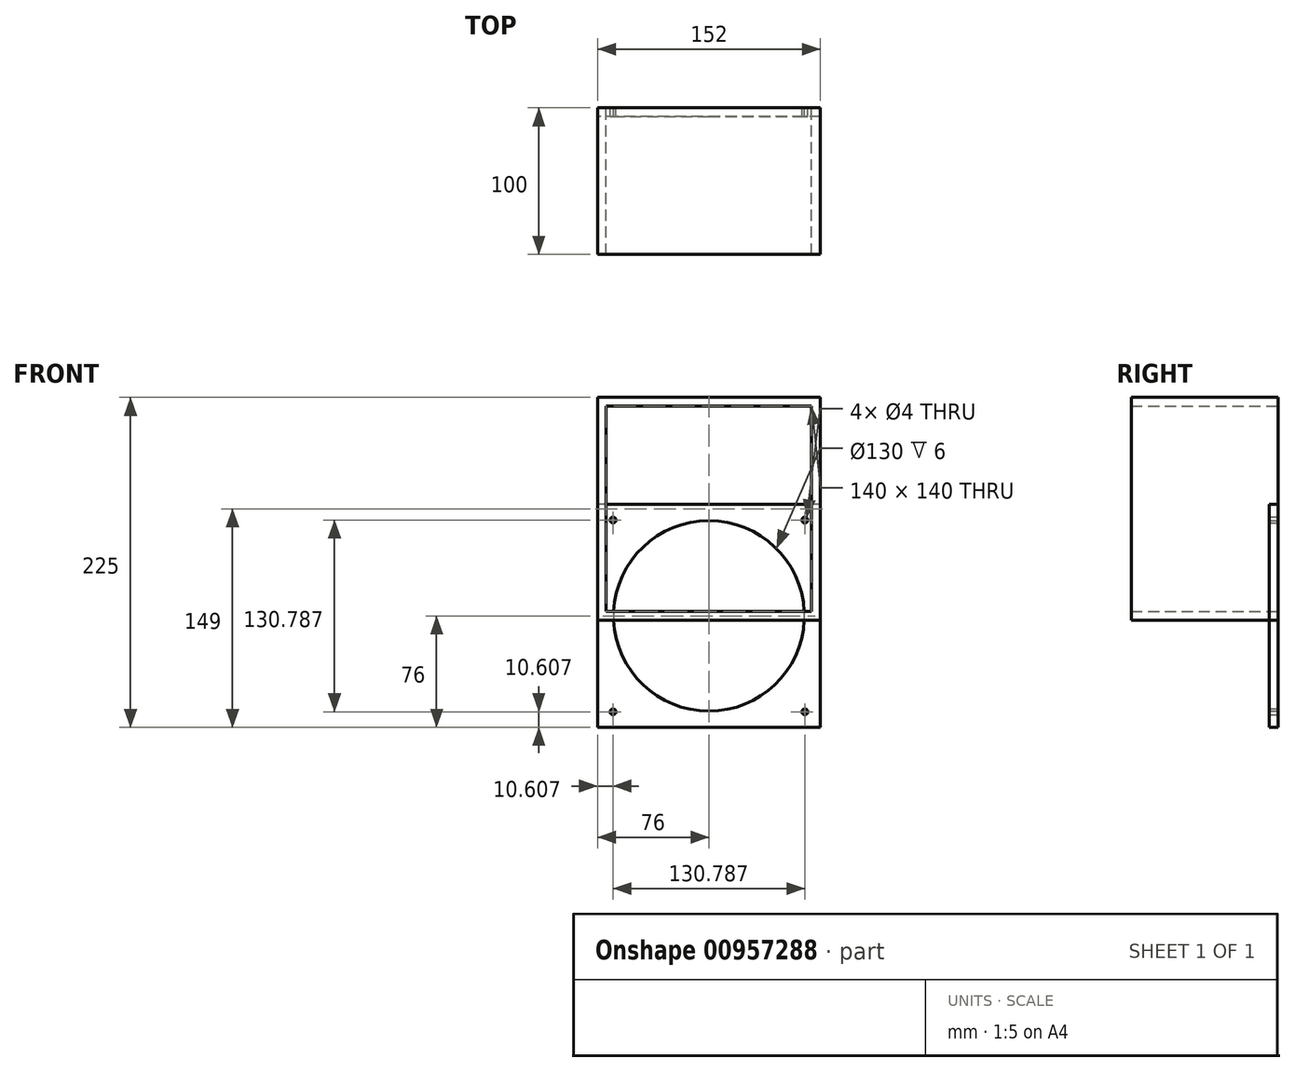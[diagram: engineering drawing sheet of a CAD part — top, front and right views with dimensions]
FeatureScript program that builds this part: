
annotation { "Feature Type Name" : "Feature", "Feature Type Description" : "" }
export const myFeature = defineFeature(function(context is Context, id is Id, definition is map)
    precondition{}
    {
        {
            var Q0;
            Q0=qCreatedBy(makeId("Front.planeOp"),FACE);
            var sketch = newSketch(context, id + "F0", { "sketchPlane" : qUnion([Q0])});
            skLineSegment(sketch, "E0.bottom", {"start": v(70, 3) * mm, "end": v(-70, 3) * mm});
            skLineSegment(sketch, "E0.top", {"start": v(70, -3) * mm, "end": v(-70, -3) * mm});
            skLineSegment(sketch, "E0.left", {"start": v(70, 3) * mm, "end": v(70, -3) * mm});
            skLineSegment(sketch, "E0.right", {"start": v(-70, 3) * mm, "end": v(-70, -3) * mm});
            skPoint(sketch, "E0.middle", {"position": v(0, 0) * mm});
            skLineSegment(sketch, "E1.bottom", {"start": v(70, -3) * mm, "end": v(76, -3) * mm});
            skLineSegment(sketch, "E1.top", {"start": v(70, 149) * mm, "end": v(76, 149) * mm});
            skLineSegment(sketch, "E1.left", {"start": v(70, -3) * mm, "end": v(70, 149) * mm});
            skLineSegment(sketch, "E1.right", {"start": v(76, -3) * mm, "end": v(76, 149) * mm});
            skPoint(sketch, "E2.oppositeSnap0", {"position": v(73, 149) * mm});
            skLineSegment(sketch, "E2.bottom", {"start": v(-70, -3) * mm, "end": v(-76, -3) * mm});
            skLineSegment(sketch, "E2.top", {"start": v(-70, 149) * mm, "end": v(-76, 149) * mm});
            skLineSegment(sketch, "E2.left", {"start": v(-70, -3) * mm, "end": v(-70, 149) * mm});
            skLineSegment(sketch, "E2.right", {"start": v(-76, -3) * mm, "end": v(-76, 149) * mm});
            skLineSegment(sketch, "E3.bottom", {"start": v(-70, 149) * mm, "end": v(70, 149) * mm});
            skLineSegment(sketch, "E3.top", {"start": v(-70, 143) * mm, "end": v(70, 143) * mm});
            skLineSegment(sketch, "E3.left", {"start": v(-70, 149) * mm, "end": v(-70, 143) * mm});
            skLineSegment(sketch, "E3.right", {"start": v(70, 149) * mm, "end": v(70, 143) * mm});
            skSolve(sketch);
        }
        {
            var Q0;
            {var subQ3=sQuery(id+"F0.wireOp",EDGE,"E2.bottom");Q0=makeQuery(id+"F0.imprint","IMPRINT",FACE,{"disambiguationData":[TD([[makeQuery(id+"F0.imprint","IMPRINT",EDGE,{"derivedFrom":subQ3}),-1.0]])]});}
            var Q1;
            Q1=makeQuery(id+"F0.imprint","IMPRINT",FACE,{"disambiguationData":[TD([[makeQuery(id+"F0.imprint","IMPRINT",EDGE,{"derivedFrom":sQuery(id+"F0.wireOp",EDGE,"E3.bottom")}),-1.0]])]});
            var Q2;
            {var subQ3=sQuery(id+"F0.wireOp",EDGE,"E1.bottom");Q2=makeQuery(id+"F0.imprint","IMPRINT",FACE,{"disambiguationData":[TD([[makeQuery(id+"F0.imprint","IMPRINT",EDGE,{"derivedFrom":subQ3}),1.0]])]});}
            var Q3;
            {var subQ0=sQuery(id+"F0.wireOp",EDGE,"E0.bottom");Q3=makeQuery(id+"F0.imprint","IMPRINT",FACE,{"disambiguationData":[TD([[makeQuery(id+"F0.imprint","IMPRINT",EDGE,{"derivedFrom":subQ0}),1.0]])]});}
            extrude(context, id + "F1", {"entities" : qUnion([Q0, Q1, Q2, Q3]), "depth" : 100 * mm, "offsetDistance" : 25 * mm});
        }
        {
            var Q0;
            Q0=qCreatedBy(makeId("Front.planeOp"),FACE);
            var sketch = newSketch(context, id + "F2", { "sketchPlane" : qUnion([Q0])});
            skLineSegment(sketch, "E4.bottom", {"start": v(76, 76) * mm, "end": v(-76, 76) * mm});
            skLineSegment(sketch, "E4.top", {"start": v(76, -76) * mm, "end": v(-76, -76) * mm});
            skLineSegment(sketch, "E4.left", {"start": v(76, 76) * mm, "end": v(76, -76) * mm});
            skLineSegment(sketch, "E4.right", {"start": v(-76, 76) * mm, "end": v(-76, -76) * mm});
            skPoint(sketch, "E4.middle", {"position": v(0, 0) * mm});
            skCircle(sketch, "E5", {"center": v(0, 0) * mm, "radius": 65 * mm});
            skLineSegment(sketch, "E6", {"start": v(-76, -76) * mm, "end": v(-65.4, -65.4) * mm});
            skLineSegment(sketch, "E7", {"start": v(76, -76) * mm, "end": v(65.4, -65.4) * mm});
            skLineSegment(sketch, "E8", {"start": v(-76, 76) * mm, "end": v(-65.4, 65.4) * mm});
            skLineSegment(sketch, "E9", {"start": v(76, 76) * mm, "end": v(65.4, 65.4) * mm});
            skCircle(sketch, "E10", {"center": v(65.4, -65.4) * mm, "radius": 2 * mm});
            skCircle(sketch, "E11", {"center": v(-65.4, -65.4) * mm, "radius": 2 * mm});
            skCircle(sketch, "E12", {"center": v(65.4, 65.4) * mm, "radius": 2 * mm});
            skCircle(sketch, "E13", {"center": v(-65.4, 65.4) * mm, "radius": 2 * mm});
            skSolve(sketch);
        }
        {
            var Q0;
            Q0=makeQuery(id+"F2.imprint","IMPRINT",FACE,{"disambiguationData":[TD([[makeQuery(id+"F2.imprint","IMPRINT",EDGE,{"derivedFrom":sQuery(id+"F2.wireOp",EDGE,"E4.bottom")}),1.0]])]});
            extrude(context, id + "F3", {"entities" : qUnion([Q0]), "depth" : 6 * mm, "offsetDistance" : 25 * mm});
        }
    });
